# Revit family: KingswayGroup_ElctrcStrksAndFcplts_HighSecureElectricStrikeRelease
name_source: partatom
category: Specialty Equipment
units: mm (PartAtom-declared; Revit-internal decimal feet)

## family parameters
Always vertical = No
Cut with Voids When Loaded = No
Part Type = Normal
Room Calculation Point = No
Round Connector Dimension = Use Diameter
Shared = No
Work Plane-Based = No

## types (1)
- KingswayGroup_ElctrcStrksAndFcplts_HighSecureElectricStrikeRelease
    AssetType = Fixed
    BIMObjectName = KingswayGroup_ElectricStrikesAndFaceplates_HighSecureElectricStrikeRelease
    BaseMaterial = NBS_Concept
    Category = Pr_75_30_27_26:Electric strikes and faceplates
    Color = For full range of available finishes and colours, contact Kingsway Group
    Default Elevation = 0 mm  [stored 0 ft]
    Description = High Secure Electric Strike Release
    DurationUnit = year
    Features = An electric strike release designed for high secure environments, providing the solution where security is a key consideration and access is to be permitted by authorised persons only. It can be operated by a wall mounted switch or a staff fob, as well as automatically unlocked during fire alarms. The KG240M version has the ability to monitor whether the door is engaged and can detect tampering to its release device.
    Finish = For full range of available finishes and colours, contact Kingsway Group
    IfcExportAs = IfcDiscreteAccessoryType
    IfcExportType = USERDEFINED
    Manufacturer = Kingsway Group
    ManufacturerName = Kingsway Group
    ManufacturerURL = https://kingswaygroupglobal.com
    Material = For full range of available material, contact Kingsway Group
    Model = KG240
    ModelNumber = KG240
    ModelReference = High Secure Electric Strike Release
    Name = ElectricStrikesAndFaceplates_HighSecureElectricStrikeRelease_KG240_KingswayGroup
    NominalHeight = 175 mm  [stored 0.574147 ft]
    NominalLength = 45 mm
    NominalWidth = 25 mm  [stored 0.082021 ft]
    PlateMaterial = NBS_Concept
    ProductInformation = https://kingswaygroupglobal.com
    Size = 44.5 x 175 x 25 mm
    URL = https://kingswaygroupglobal.com
    Uniclass2015Code = Pr_75_30_27_26
    Uniclass2015Title = Electric strikes and faceplates
    Uniclass2015Version = Products v1.36
    Version = 1
    WarrantyDescription = 5-Year Guarantee *For faulty manufacture and not for damage
    WarrantyDurationParts = 5
    WarrantyDurationUnit = year

note: [stored X ft] marks values corroborated as IEEE doubles in the binary element streams (Revit-internal decimal feet)

## geometry (parser evidence)
native form markers: Sweep x2
no freeform markers — native parametric forms only
